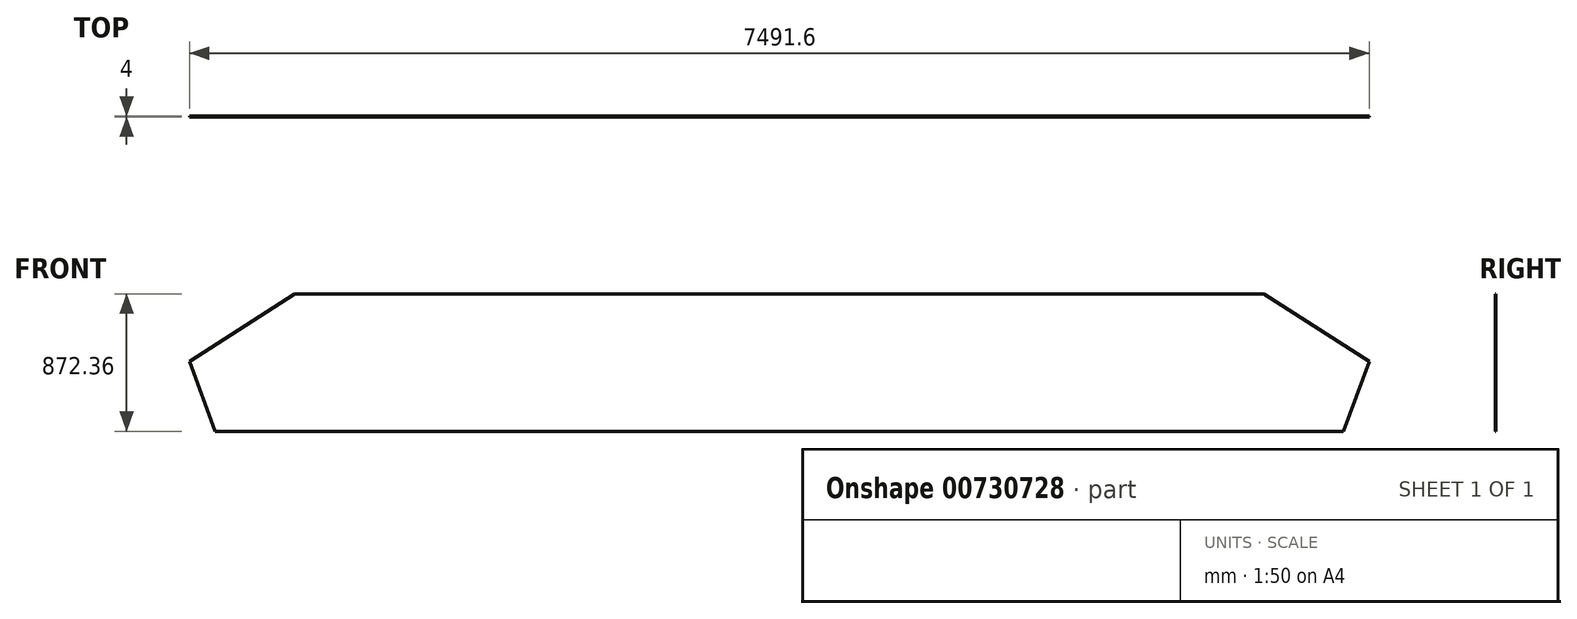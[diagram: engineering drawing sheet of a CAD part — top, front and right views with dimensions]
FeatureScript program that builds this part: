
annotation { "Feature Type Name" : "Feature", "Feature Type Description" : "" }
export const myFeature = defineFeature(function(context is Context, id is Id, definition is map)
    precondition{}
    {
        {
            var Q0;
            Q0=qCreatedBy(makeId("Front.planeOp"),FACE);
            var sketch = newSketch(context, id + "F0", { "sketchPlane" : qUnion([Q0])});
            skLineSegment(sketch, "E0", {"start": v(-3583.4, -436.18) * mm, "end": v(-3745.8, 7.99) * mm});
            skLineSegment(sketch, "E1", {"start": v(-3745.8, 7.99) * mm, "end": v(-3077.93, 436.18) * mm});
            skLineSegment(sketch, "E2", {"start": v(-3077.93, 436.18) * mm, "end": v(-0.01, 436.18) * mm});
            skLineSegment(sketch, "E3", {"start": v(-0.01, 436.18) * mm, "end": v(-0.01, 309.18) * mm});
            skLineSegment(sketch, "E4", {"start": v(-0.01, 309.18) * mm, "end": v(-0.01, 436.18) * mm});
            skLineSegment(sketch, "E5", {"start": v(-0.01, 436.18) * mm, "end": v(3077.93, 436.18) * mm});
            skLineSegment(sketch, "E6", {"start": v(3077.93, 436.18) * mm, "end": v(3745.8, 7.99) * mm});
            skLineSegment(sketch, "E7", {"start": v(3745.8, 7.99) * mm, "end": v(3583.4, -436.18) * mm});
            skLineSegment(sketch, "E8", {"start": v(3583.4, -436.18) * mm, "end": v(-0.01, -436.18) * mm});
            skLineSegment(sketch, "E9", {"start": v(-0.01, -436.18) * mm, "end": v(-0.01, -309.18) * mm});
            skLineSegment(sketch, "E10", {"start": v(-0.01, -309.18) * mm, "end": v(-0.01, -436.18) * mm});
            skLineSegment(sketch, "E11", {"start": v(-0.01, -436.18) * mm, "end": v(-3583.4, -436.18) * mm});
            skSolve(sketch);
        }
        {
            var Q0;
            Q0 = qSketchRegion(id + "F0", true);
            extrude(context, id + "F1", {"entities" : qUnion([Q0]), "depth" : 4 * mm, "offsetDistance" : 25 * mm});
        }
    });
